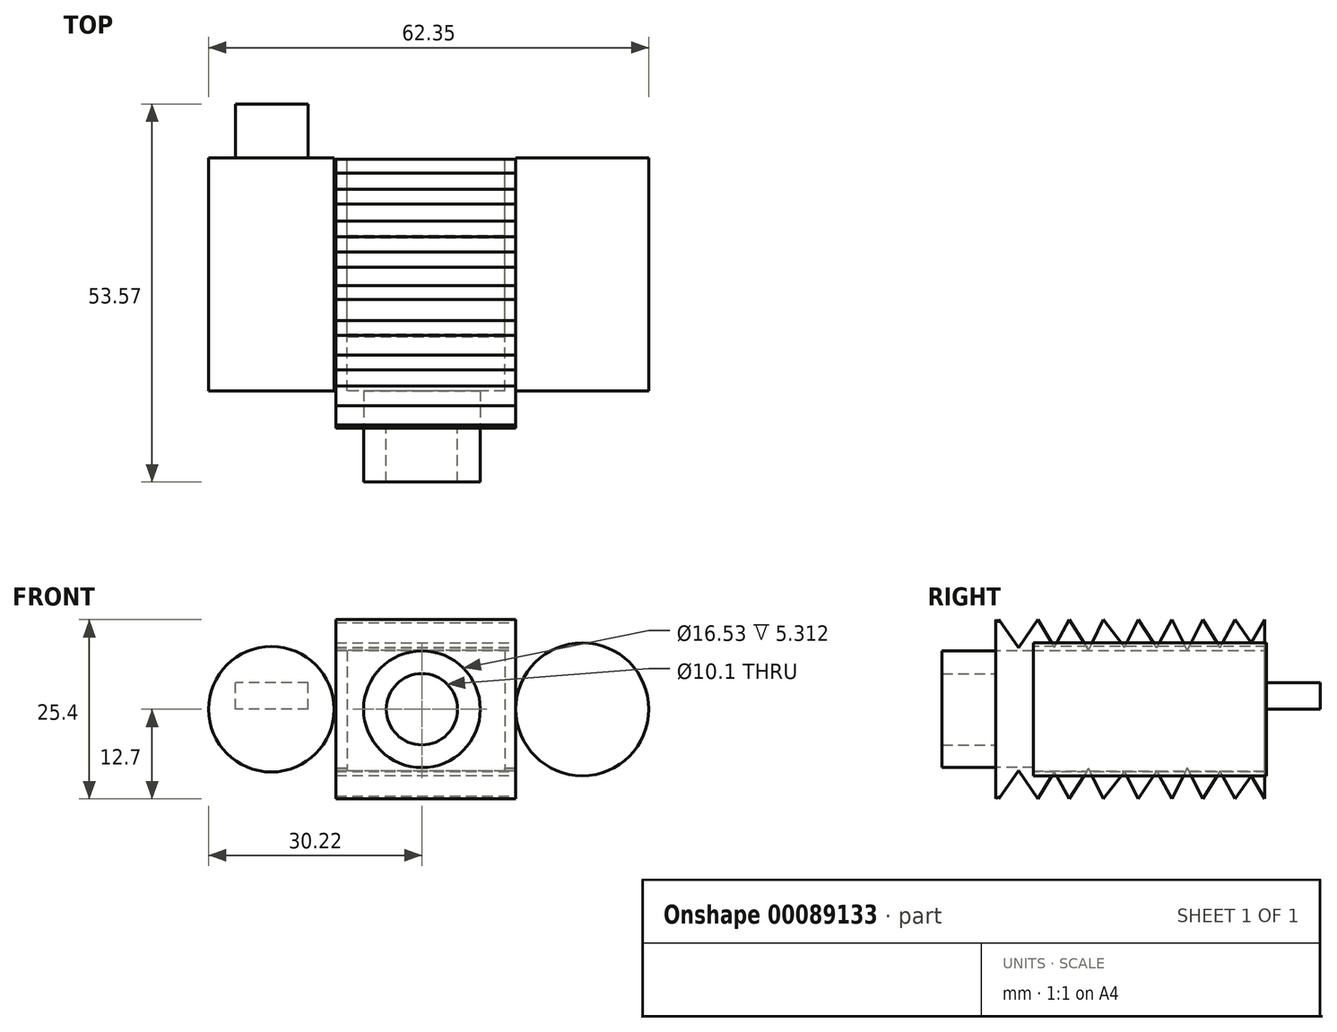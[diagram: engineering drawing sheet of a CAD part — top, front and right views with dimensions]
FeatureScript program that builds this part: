
annotation { "Feature Type Name" : "Feature", "Feature Type Description" : "" }
export const myFeature = defineFeature(function(context is Context, id is Id, definition is map)
    precondition{}
    {
        {
            var Q0;
            Q0=qCreatedBy(makeId("Front.planeOp"),FACE);
            var sketch = newSketch(context, id + "F0", { "sketchPlane" : qUnion([Q0])});
            skLineSegment(sketch, "E0.bottom", {"start": v(-12.17, 0) * mm, "end": v(13.25, 0) * mm});
            skLineSegment(sketch, "E0.top", {"start": v(-12.17, 12.7) * mm, "end": v(13.25, 12.7) * mm});
            skLineSegment(sketch, "E0.left", {"start": v(-12.17, 0) * mm, "end": v(-12.17, 12.7) * mm});
            skLineSegment(sketch, "E0.right", {"start": v(13.25, 0) * mm, "end": v(13.25, 12.7) * mm});
            skSolve(sketch);
        }
        {
            var Q0;
            Q0 = qSketchRegion(id + "F0", true);
            extrude(context, id + "F1", {"entities" : qUnion([Q0]), "depth" : 38.1 * mm});
        }
        {
            var Q0;
            Q0=makeQuery(id+"F1.opExtrude","SWEPT_FACE",FACE,{"disambiguationData":[OSD([sQuery(id+"F0.wireOp",EDGE,"E0.right")])]});
            var sketch = newSketch(context, id + "F2", { "sketchPlane" : qUnion([Q0])});
            skLineSegment(sketch, "E1", {"start": v(-38.1, 12.7) * mm, "end": v(-35.87, 8.5) * mm});
            skLineSegment(sketch, "E2", {"start": v(-35.87, 8.5) * mm, "end": v(-46.16, 12.7) * mm});
            skLineSegment(sketch, "E3", {"start": v(-46.16, 12.7) * mm, "end": v(-43.63, 8.8) * mm});
            skLineSegment(sketch, "E4", {"start": v(-43.63, 8.8) * mm, "end": v(-41.76, 12.7) * mm});
            skLineSegment(sketch, "E5", {"start": v(-41.76, 12.7) * mm, "end": v(-39.6, 8.99) * mm});
            skLineSegment(sketch, "E6", {"start": v(-39.6, 8.99) * mm, "end": v(-37.67, 12.7) * mm});
            skLineSegment(sketch, "E7", {"start": v(0, 12.7) * mm, "end": v(-1.94, 9.4) * mm});
            skLineSegment(sketch, "E8", {"start": v(-1.94, 9.4) * mm, "end": v(-4.23, 12.7) * mm});
            skLineSegment(sketch, "E9", {"start": v(-4.23, 12.7) * mm, "end": v(-6.33, 8.75) * mm});
            skLineSegment(sketch, "E10", {"start": v(-6.33, 8.75) * mm, "end": v(-8.74, 12.7) * mm});
            skLineSegment(sketch, "E11", {"start": v(-8.74, 12.7) * mm, "end": v(-10.97, 8.32) * mm});
            skLineSegment(sketch, "E12", {"start": v(-10.97, 8.32) * mm, "end": v(-13.14, 12.7) * mm});
            skLineSegment(sketch, "E13", {"start": v(-13.14, 12.7) * mm, "end": v(-15.31, 8.69) * mm});
            skLineSegment(sketch, "E14", {"start": v(-15.31, 8.69) * mm, "end": v(-17.9, 12.7) * mm});
            skLineSegment(sketch, "E15", {"start": v(-17.9, 12.7) * mm, "end": v(-19.9, 8.8) * mm});
            skLineSegment(sketch, "E16", {"start": v(-19.9, 8.8) * mm, "end": v(-22.84, 12.7) * mm});
            skLineSegment(sketch, "E17", {"start": v(-22.84, 12.7) * mm, "end": v(-24.95, 8.39) * mm});
            skLineSegment(sketch, "E18", {"start": v(-24.95, 8.39) * mm, "end": v(-27.72, 12.7) * mm});
            skLineSegment(sketch, "E19", {"start": v(-27.72, 12.7) * mm, "end": v(-29.83, 8.8) * mm});
            skLineSegment(sketch, "E20", {"start": v(-29.83, 8.8) * mm, "end": v(-32.12, 12.7) * mm});
            skLineSegment(sketch, "E21", {"start": v(-32.12, 12.7) * mm, "end": v(-34.9, 8.69) * mm});
            skLineSegment(sketch, "E22", {"start": v(-34.9, 8.69) * mm, "end": v(-37.67, 12.7) * mm});
            skSolve(sketch);
        }
        {
            var Q0;
            {var subQ0=sQuery(id+"F2.wireOp",EDGE,"E5");Q0=makeQuery(id+"F2.imprint","IMPRINT",FACE,{"disambiguationData":[TD([[makeQuery(id+"F2.imprint","IMPRINT",EDGE,{"derivedFrom":subQ0}),1.0]])]});}
            var Q1;
            {var subQ0=sQuery(id+"F2.wireOp",EDGE,"E1");Q1=makeQuery(id+"F2.imprint","IMPRINT",FACE,{"disambiguationData":[TD([[makeQuery(id+"F2.imprint","IMPRINT",EDGE,{"derivedFrom":subQ0}),1.0]])]});}
            var Q2;
            {var subQ0=sQuery(id+"F2.wireOp",EDGE,"E15");Q2=makeQuery(id+"F2.imprint","IMPRINT",FACE,{"disambiguationData":[TD([[makeQuery(id+"F2.imprint","IMPRINT",EDGE,{"derivedFrom":subQ0}),-1.0]])]});}
            var Q3;
            {var subQ0=sQuery(id+"F2.wireOp",EDGE,"E3");Q3=makeQuery(id+"F2.imprint","IMPRINT",FACE,{"disambiguationData":[TD([[makeQuery(id+"F2.imprint","IMPRINT",EDGE,{"derivedFrom":subQ0}),1.0]])]});}
            var Q4;
            {var subQ0=sQuery(id+"F2.wireOp",EDGE,"E11");Q4=makeQuery(id+"F2.imprint","IMPRINT",FACE,{"disambiguationData":[TD([[makeQuery(id+"F2.imprint","IMPRINT",EDGE,{"derivedFrom":subQ0}),-1.0]])]});}
            var Q5;
            {var subQ0=sQuery(id+"F2.wireOp",EDGE,"E19");Q5=makeQuery(id+"F2.imprint","IMPRINT",FACE,{"disambiguationData":[TD([[makeQuery(id+"F2.imprint","IMPRINT",EDGE,{"derivedFrom":subQ0}),-1.0]])]});}
            var Q6;
            {var subQ0=sQuery(id+"F2.wireOp",EDGE,"E7");Q6=makeQuery(id+"F2.imprint","IMPRINT",FACE,{"disambiguationData":[TD([[makeQuery(id+"F2.imprint","IMPRINT",EDGE,{"derivedFrom":subQ0}),-1.0]])]});}
            var Q7;
            {var subQ0=sQuery(id+"F2.wireOp",EDGE,"E13");Q7=makeQuery(id+"F2.imprint","IMPRINT",FACE,{"disambiguationData":[TD([[makeQuery(id+"F2.imprint","IMPRINT",EDGE,{"derivedFrom":subQ0}),-1.0]])]});}
            var Q8;
            {var subQ0=sQuery(id+"F2.wireOp",EDGE,"E21");Q8=makeQuery(id+"F2.imprint","IMPRINT",FACE,{"disambiguationData":[TD([[makeQuery(id+"F2.imprint","IMPRINT",EDGE,{"derivedFrom":subQ0}),-1.0]])]});}
            var Q9;
            {var subQ0=sQuery(id+"F2.wireOp",EDGE,"E9");Q9=makeQuery(id+"F2.imprint","IMPRINT",FACE,{"disambiguationData":[TD([[makeQuery(id+"F2.imprint","IMPRINT",EDGE,{"derivedFrom":subQ0}),-1.0]])]});}
            var Q10;
            {var subQ0=sQuery(id+"F2.wireOp",EDGE,"E17");Q10=makeQuery(id+"F2.imprint","IMPRINT",FACE,{"disambiguationData":[TD([[makeQuery(id+"F2.imprint","IMPRINT",EDGE,{"derivedFrom":subQ0}),-1.0]])]});}
            extrude(context, id + "F3", {"entities" : qUnion([Q0, Q1, Q2, Q3, Q4, Q5, Q6, Q7, Q8, Q9, Q10]), "operationType" : NewBodyOperationType.REMOVE, "oppositeDirection" : true, "depth" : 127 * mm});
        }
        {
            var Q0;
            Q0=makeQuery(id+"F1.opExtrude","SWEPT_BODY",BODY,{"disambiguationData":[OSD([sQuery(id+"F0.wireOp",EDGE,"E0.bottom"),sQuery(id+"F0.wireOp",EDGE,"E0.top"),sQuery(id+"F0.wireOp",EDGE,"E0.left"),sQuery(id+"F0.wireOp",EDGE,"E0.right")])]});
            var Q1;
            Q1=makeQuery(id+"F1.opExtrude","SWEPT_FACE",FACE,{"disambiguationData":[OSD([sQuery(id+"F0.wireOp",EDGE,"E0.bottom")])]});
            mirror(context, id + "F4", {"operationType" : NewBodyOperationType.ADD, "entities" : qUnion([Q0]), "mirrorPlane" : qUnion([Q1])});
        }
        {
            var Q0;
            {var subQ0=makeQuery(id+"F1.opExtrude","CAP_FACE",FACE,{"disambiguationData":[OSD([sQuery(id+"F0.wireOp",EDGE,"E0.bottom"),sQuery(id+"F0.wireOp",EDGE,"E0.top"),sQuery(id+"F0.wireOp",EDGE,"E0.left"),sQuery(id+"F0.wireOp",EDGE,"E0.right")])],"isStart":false});Q0=makeQuery(id+"F4.boolean.opBoolean","MERGE",FACE,{"derivedFrom":[subQ0,makeQuery(id+"F4.opPattern","COPY",FACE,{"derivedFrom":subQ0,"instanceName":"1"})]});}
            var sketch = newSketch(context, id + "F5", { "sketchPlane" : qUnion([Q0])});
            skCircle(sketch, "E23", {"center": v(0, 0) * mm, "radius": 8.27 * mm});
            skSolve(sketch);
        }
        {
            var Q0;
            Q0=makeQuery(id+"F5.imprint","IMPRINT",FACE,{"disambiguationData":[TD([[makeQuery(id+"F5.imprint","IMPRINT",EDGE,{"derivedFrom":sQuery(id+"F5.wireOp",EDGE,"E23")}),1.0]])]});
            var sketch = newSketch(context, id + "F6", { "sketchPlane" : qUnion([Q0])});
            skCircle(sketch, "E24", {"center": v(0, 0) * mm, "radius": 5.05 * mm});
            skSolve(sketch);
        }
        {
            var Q0;
            Q0=makeQuery(id+"F6.imprint","IMPRINT",FACE,{"disambiguationData":[TD([[makeQuery(id+"F6.imprint","IMPRINT",EDGE,{"derivedFrom":sQuery(id+"F6.wireOp",EDGE,"E24")}),-1.0]])]});
            extrude(context, id + "F7", {"entities" : qUnion([Q0]), "operationType" : NewBodyOperationType.ADD, "depth" : 7.62 * mm});
        }
        {
            var Q0;
            Q0=makeQuery(id+"F5.imprint","IMPRINT",FACE,{"disambiguationData":[TD([[makeQuery(id+"F5.imprint","IMPRINT",EDGE,{"derivedFrom":sQuery(id+"F5.wireOp",EDGE,"E23")}),1.0]])]});
            extrude(context, id + "F8", {"entities" : qUnion([Q0]), "operationType" : NewBodyOperationType.REMOVE, "oppositeDirection" : true, "depth" : 508 * mm});
        }
        {
            var Q0;
            {var subQ0=makeQuery(id+"F1.opExtrude","CAP_FACE",FACE,{"disambiguationData":[OSD([sQuery(id+"F0.wireOp",EDGE,"E0.bottom"),sQuery(id+"F0.wireOp",EDGE,"E0.top"),sQuery(id+"F0.wireOp",EDGE,"E0.left"),sQuery(id+"F0.wireOp",EDGE,"E0.right")])],"isStart":true});Q0=makeQuery(id+"F4.boolean.opBoolean","MERGE",FACE,{"derivedFrom":[subQ0,makeQuery(id+"F4.opPattern","COPY",FACE,{"derivedFrom":subQ0,"instanceName":"1"})]});}
            var sketch = newSketch(context, id + "F9", { "sketchPlane" : qUnion([Q0])});
            skLineSegment(sketch, "E25.bottom", {"start": v(-11.75, 8.32) * mm, "end": v(10.6, 8.32) * mm});
            skLineSegment(sketch, "E25.top", {"start": v(-11.75, -8.73) * mm, "end": v(10.6, -8.73) * mm});
            skLineSegment(sketch, "E25.left", {"start": v(-11.75, 8.32) * mm, "end": v(-11.75, -8.73) * mm});
            skLineSegment(sketch, "E25.right", {"start": v(10.6, 8.32) * mm, "end": v(10.6, -8.73) * mm});
            skSolve(sketch);
        }
        {
            var Q0;
            Q0=makeQuery(id+"F9.imprint","IMPRINT",FACE,{"disambiguationData":[TD([[makeQuery(id+"F9.imprint","IMPRINT",EDGE,{"derivedFrom":sQuery(id+"F9.wireOp",EDGE,"E25.bottom")}),-1.0]])]});
            extrude(context, id + "F10", {"entities" : qUnion([Q0]), "operationType" : NewBodyOperationType.REMOVE, "oppositeDirection" : true, "depth" : 32.8 * mm});
        }
        {
            var Q0;
            Q0=makeQuery(id+"F10.boolean.opBoolean","COPY",FACE,{"derivedFrom":makeQuery(id+"F10.opExtrude","CAP_FACE",FACE,{"disambiguationData":[OSD([sQuery(id+"F0.wireOp",EDGE,"E0.bottom"),sQuery(id+"F0.wireOp",EDGE,"E0.top"),sQuery(id+"F0.wireOp",EDGE,"E0.left"),sQuery(id+"F0.wireOp",EDGE,"E0.right"),sQuery(id+"F5.wireOp",EDGE,"E23"),sQuery(id+"F9.wireOp",EDGE,"E25.bottom"),sQuery(id+"F9.wireOp",EDGE,"E25.top"),sQuery(id+"F9.wireOp",EDGE,"E25.left"),sQuery(id+"F9.wireOp",EDGE,"E25.right")])],"isStart":false})});
            var sketch = newSketch(context, id + "F11", { "sketchPlane" : qUnion([Q0])});
            skCircle(sketch, "E26", {"center": v(-22.71, 0) * mm, "radius": 9.42 * mm});
            skCircle(sketch, "E27", {"center": v(21.33, 0) * mm, "radius": 8.9 * mm});
            skSolve(sketch);
        }
        {
            var Q0;
            Q0=makeQuery(id+"F11.imprint","IMPRINT",FACE,{"disambiguationData":[TD([[makeQuery(id+"F11.imprint","IMPRINT",EDGE,{"derivedFrom":sQuery(id+"F11.wireOp",EDGE,"E26")}),1.0]])]});
            extrude(context, id + "F12", {"entities" : qUnion([Q0]), "depth" : 33.02 * mm});
        }
        {
            var Q0;
            Q0=makeQuery(id+"F11.imprint","IMPRINT",FACE,{"disambiguationData":[TD([[makeQuery(id+"F11.imprint","IMPRINT",EDGE,{"derivedFrom":sQuery(id+"F11.wireOp",EDGE,"E27")}),1.0]])]});
            extrude(context, id + "F13", {"entities" : qUnion([Q0]), "depth" : 33.02 * mm});
        }
        {
            var Q0;
            Q0=makeQuery(id+"F13.opExtrude","CAP_FACE",FACE,{"disambiguationData":[OSD([sQuery(id+"F11.wireOp",EDGE,"E27")])],"isStart":false});
            var sketch = newSketch(context, id + "F14", { "sketchPlane" : qUnion([Q0])});
            skLineSegment(sketch, "E28.bottom", {"start": v(16.12, 0) * mm, "end": v(26.41, 0) * mm});
            skLineSegment(sketch, "E28.top", {"start": v(16.12, 3.78) * mm, "end": v(26.41, 3.78) * mm});
            skLineSegment(sketch, "E28.left", {"start": v(16.12, 0) * mm, "end": v(16.12, 3.78) * mm});
            skLineSegment(sketch, "E28.right", {"start": v(26.41, 0) * mm, "end": v(26.41, 3.78) * mm});
            skLineSegment(sketch, "E29.bottom", {"start": v(26.41, 0) * mm, "end": v(16.2, 0) * mm});
            skLineSegment(sketch, "E29.top", {"start": v(26.41, -3.68) * mm, "end": v(16.2, -3.68) * mm});
            skLineSegment(sketch, "E29.left", {"start": v(26.41, 0) * mm, "end": v(26.41, -3.68) * mm});
            skLineSegment(sketch, "E29.right", {"start": v(16.2, 0) * mm, "end": v(16.2, -3.68) * mm});
            skSolve(sketch);
        }
        {
            var Q0;
            Q0=makeQuery(id+"F14.imprint","IMPRINT",FACE,{"disambiguationData":[TD([[makeQuery(id+"F14.imprint","IMPRINT",EDGE,{"derivedFrom":sQuery(id+"F14.wireOp",EDGE,"E29.bottom")}),1.0]])]});
            var Q1;
            Q1=makeQuery(id+"F14.imprint","IMPRINT",FACE,{"disambiguationData":[TD([[makeQuery(id+"F14.imprint","IMPRINT",EDGE,{"derivedFrom":sQuery(id+"F14.wireOp",EDGE,"E28.bottom")}),1.0]])]});
            extrude(context, id + "F15", {"entities" : qUnion([Q0, Q1]), "operationType" : NewBodyOperationType.ADD, "depth" : 7.62 * mm});
        }
        {
            var Q0;
            Q0=makeQuery(id+"F15.opExtrude","SWEPT_FACE",FACE,{"disambiguationData":[OSD([sQuery(id+"F14.wireOp",EDGE,"E28.left")])]});
            var sketch = newSketch(context, id + "F16", { "sketchPlane" : qUnion([Q0])});
            skPoint(sketch, "E30.oppositeSnap0", {"position": v(4.04, 0) * mm});
            skLineSegment(sketch, "E30.bottom", {"start": v(4.04, 0) * mm, "end": v(4.04, 0) * mm});
            skLineSegment(sketch, "E30.top", {"start": v(4.04, 1.08) * mm, "end": v(4.04, 1.08) * mm});
            skLineSegment(sketch, "E30.left", {"start": v(4.04, 0) * mm, "end": v(4.04, 1.08) * mm});
            skLineSegment(sketch, "E30.right", {"start": v(4.04, 0) * mm, "end": v(4.04, 1.08) * mm});
            skLineSegment(sketch, "E31.top", {"start": v(4.04, -1.13) * mm, "end": v(4.04, -1.13) * mm});
            skLineSegment(sketch, "E31.left", {"start": v(4.04, 0) * mm, "end": v(4.04, -1.13) * mm});
            skLineSegment(sketch, "E31.right", {"start": v(4.04, 0) * mm, "end": v(4.04, -1.13) * mm});
            skSolve(sketch);
        }
        {
            var Q0;
            Q0=sQuery(id+"F16.wireOp",EDGE,"E30.right");
            var Q1;
            Q1=sQuery(id+"F16.wireOp",EDGE,"E31.right");
            extrude(context, id + "F17", {"bodyType" : ToolBodyType.SURFACE, "surfaceEntities" : qUnion([Q0, Q1]), "depth" : 2.54 * mm});
        }
    });
